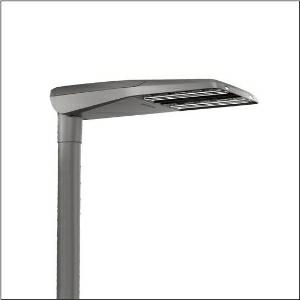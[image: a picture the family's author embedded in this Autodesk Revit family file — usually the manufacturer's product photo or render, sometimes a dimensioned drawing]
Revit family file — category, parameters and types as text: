
# Revit family: streetlight_sl_11_iq_midi___st1_2a_5xc3a31f08me_35e9
name_source: partatom
category: Lighting Fixtures
units: mm (PartAtom-declared; Revit-internal decimal feet)

## family parameters
Cut with Voids When Loaded = No
Host = Face
Light Source = No
Part Type = Normal
Room Calculation Point = No
Round Connector Dimension = Use Diameter
Shared = No

## types (1)
- --- (1 x LED, 15580 lm, 124.7 W, 3000K)
    Apparent Load = 125 VA
    CIE Flux Codes = 32 70 96 100 100
    Color Rendering = 80
    Color Temperature = 3000K
    Default Elevation = 1800 mm
    Description = Streetlight SL 11 iQ midi, mast luminaire, primary light control with 3 zone facetted reflector, of plastic, silver coated, highly specular, primary optical cover: cover, of PMMA, transparent, light distribution: ST1.2a, light emission: direct distribution, primary light characteristic: asymmetric, installation type: post-top, side-entry, LED, High Power LED, rated luminous flux: 15.580lm, luminous efficacy: 125lm/W, light colour: 830, colour temperature: 3000K, control: Street-Remote, optimised constant luminous flux control (CLO 2.0), Desk-Remote (wireless, voltage-free reading and setting of iQ features in the workshop via application-optimized NFC function/RFID function), Light-Fading, Smart-Wire, Night-Set, Lumen-Switch, Temp-Guard, Auto-Match, with cable H07RN-F 5x 1.5mm², mains connection: 220..240V, AC, 50/60Hz, connection cable pre-assembled, cable length: 12,5m, start of lifetime: 125W, end of lifetime: 132W, reduction: 57W, luminaire housing, of diecast aluminium, powder-coated, Siteco® metallic grey (DB 702S), length: 780mm, width: 376mm, height: 118mm, spigot size: 60/76mm (post-top) and 42/60/76mm (side-entry), mast flange for spigot size: 42mm: 5XC10008XM4, 60mm: 5XC10008XM2, 76/60mm: 5XC10108XM1, equipment: Power, protection rating (complete): IP66, insulation class (complete): insulation class II (safety insulation), certification: CE, ENEC, VDE, impact resistance: IK09, permissible operating ambient temperature for outdoor applications: -25..+50°C, standard-compliant lighting for roads and squares, packaging unit: 1 piece

Light Distribution: ST1.2a
    Height = 118 mm
    Lamp = 1 x LED
    Lamp Light Flux = 15580 lm
    Lamp Power = 124.7 W
    Lamp count = 1
    Length = 780 mm
    Luminous efficacy = 125 lm/W
    Manufacturer = Siteco
    ModVariant = No
    Model = 5XC3A31F08ME
    Number of Poles = 1
    OnlyDefault = Yes
    Power Factor = 1
    Product Name = Streetlight SL 11 iQ midi | ST1.2a
    Product group = mast luminaire | pylon top
    ProductGroupID = 6100
    Protection Class = Protection class II
    Protection Degree = IP 66
    RLX_Detail_Level = 1
    RlxData = <blob elided: 70413 chars, md5=313113ca>
    Socket = socket
    Standby Power = 0 W
    System Light Flux = 15580 lm
    System Power = 125 W
    Type Comments = factory setting: luminous flux: 100 % | dim-lin: 254 | 557 mA
    Type Image = l_1005960.jpg
    URL = http://relux.com
    VarID = @adj_118599
    Voltage = 0 V
    Weight = 0.00 kg
    Width = 376 mm

## geometry (parser evidence)
native form markers: Blend x4, Sweep x10
no freeform markers — native parametric forms only
